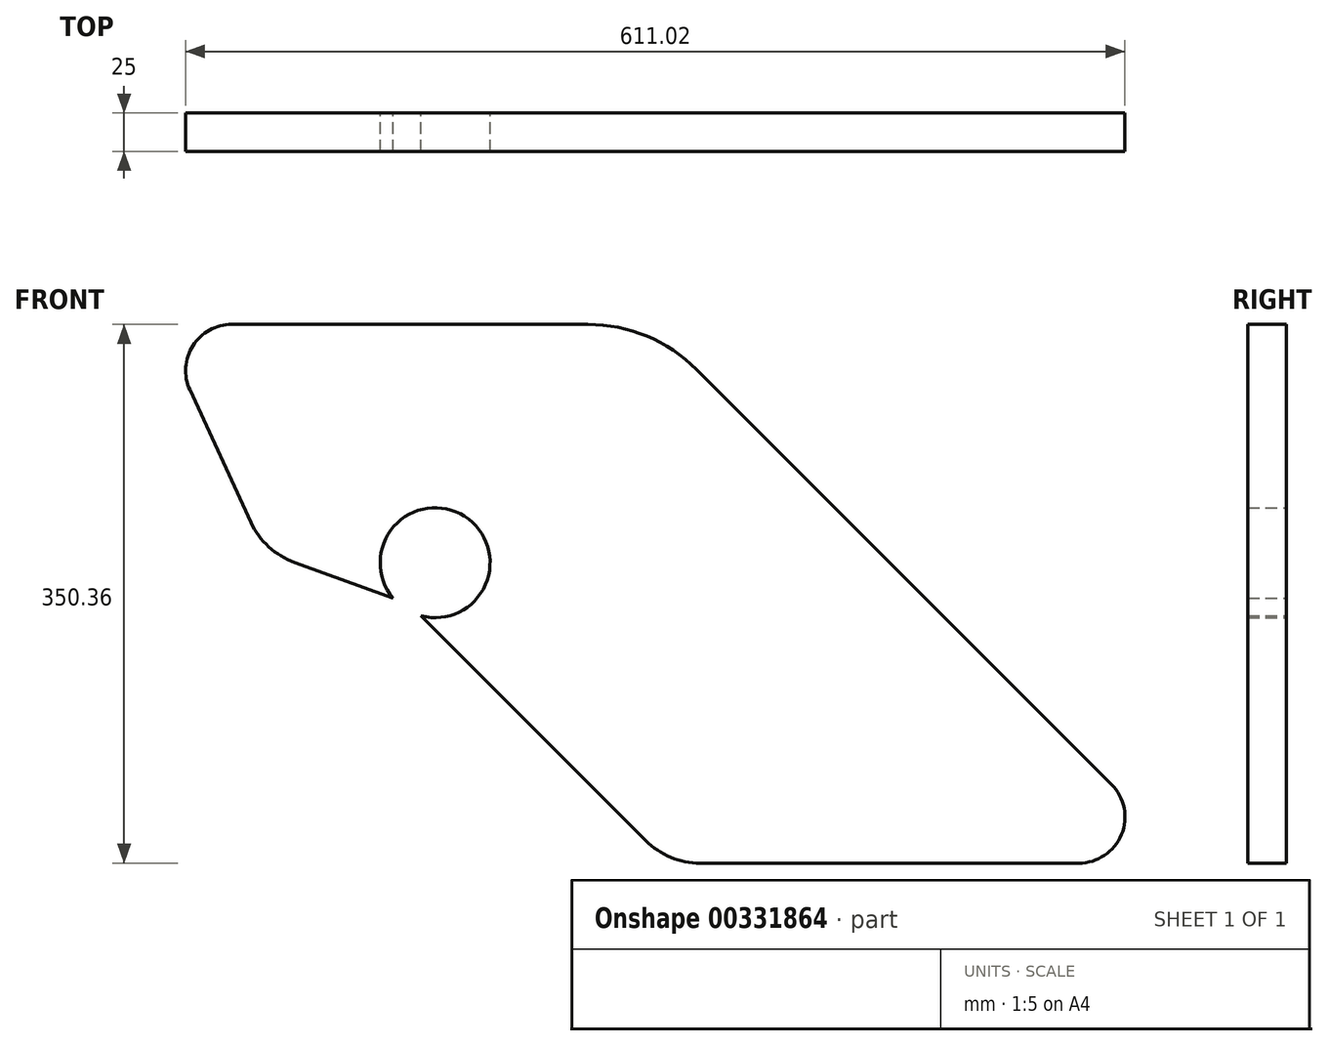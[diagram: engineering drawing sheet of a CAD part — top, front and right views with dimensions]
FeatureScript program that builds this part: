
annotation { "Feature Type Name" : "Feature", "Feature Type Description" : "" }
export const myFeature = defineFeature(function(context is Context, id is Id, definition is map)
    precondition{}
    {
        {
            var Q0;
            Q0=qCreatedBy(makeId("Front.planeOp"),FACE);
            var sketch = newSketch(context, id + "F0", { "sketchPlane" : qUnion([Q0])});
            skArc(sketch, "E0", {"start": v(-152.3, -14.36) * mm, "mid": v(-124.03, 50.37) * mm, "end": v(-170.64, -2.7) * mm});
            skLineSegment(sketch, "E1", {"start": v(-6.12, -160.53) * mm, "end": v(-152.3, -14.36) * mm});
            skArc(sketch, "E2", {"start": v(-6.12, -160.53) * mm, "mid": v(10.1, -171.37) * mm, "end": v(29.24, -175.18) * mm});
            skLineSegment(sketch, "E3", {"start": v(275.51, -175.18) * mm, "end": v(29.24, -175.18) * mm});
            skArc(sketch, "E4", {"start": v(275.51, -175.18) * mm, "mid": v(303.23, -156.66) * mm, "end": v(296.72, -123.96) * mm});
            skLineSegment(sketch, "E5", {"start": v(26.87, 145.89) * mm, "end": v(296.72, -123.96) * mm});
            skArc(sketch, "E6", {"start": v(26.87, 145.89) * mm, "mid": v(-5.57, 167.57) * mm, "end": v(-43.84, 175.18) * mm});
            skLineSegment(sketch, "E7", {"start": v(-275.51, 175.18) * mm, "end": v(-43.84, 175.18) * mm});
            skArc(sketch, "E8", {"start": v(-275.51, 175.18) * mm, "mid": v(-300.78, 161.34) * mm, "end": v(-302.75, 132.6) * mm});
            skLineSegment(sketch, "E9", {"start": v(-262.96, 46.48) * mm, "end": v(-302.75, 132.6) * mm});
            skArc(sketch, "E10", {"start": v(-262.96, 46.48) * mm, "mid": v(-251.38, 30.61) * mm, "end": v(-234.58, 20.43) * mm});
            skLineSegment(sketch, "E11", {"start": v(-170.64, -2.7) * mm, "end": v(-234.58, 20.43) * mm});
            skSolve(sketch);
        }
        {
            var Q0;
            Q0 = qSketchRegion(id + "F0", true);
            extrude(context, id + "F1", {"entities" : qUnion([Q0]), "depth" : 25 * mm});
        }
    });
